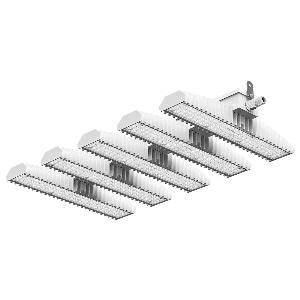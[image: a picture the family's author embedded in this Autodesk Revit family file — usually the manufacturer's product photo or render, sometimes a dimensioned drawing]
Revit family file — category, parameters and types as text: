
# Revit family: 3f_filippi_-_3f_lem_ho_ampio_3f_filippi_-_58958_-_3f_lem_5_ho_led_350_cr_ampio
name_source: partatom
category: Lighting Fixtures
units: mm (PartAtom-declared; Revit-internal decimal feet)

## family parameters
Cut with Voids When Loaded = No
Host = Face
Light Source = No
Part Type = Normal
Room Calculation Point = No
Round Connector Dimension = Use Diameter
Shared = No

## types (1)
- 3F Filippi - 3F LEM HO Ampio (1 x LED, 56516 lm, 345 W, 4000 K)
    Apparent Load = 345 VA
    Approval mark = CE
    CIE Flux Codes = 60 92 99 100 100
    Color Rendering = 80
    Color Temperature = 4000 K
    Control Gear = Electronic ballast
    Default Elevation = 1800 mm
    Description = Industrial luminaire with high light output and high luminous efficiency designed with the most innovative technologies for environments with temperature up to 55°C.

ILLUMINOTECHNICAL
Luminous efficiency 100% (DLOR 100%, ULOR 0%).
Initial luminous flux of the luminaire 56516 lm.
Direct symmetric wide distribution: the illuminated area has a rectangular shape.
Installation Interdistance Transv.D = 1.58 x hu - Long.D = 1.45 x hu.
Tabular UGR (CIE 117 - 4H-8H; S=0.25H; 70/50/20): RUG 24.2 - 25.2.
Beam angle: 93° - 99°.
Luminous efficacy 164 lm/W.
Lifetime (L93/B10): 30000 h. (tq+25°C)
Lifetime (L90/B10): 50000 h. (tq+25°C)
Lifetime (L85/B10): 80000 h. (tq+25°C)
Lifetime (L80/B10): 100000 h. (tq+25°C)
Lifetime (L85/B10): 50000 h. (tq+55°C)
Sudden decreased luminous flux after 50000 hours: 0% (C0).
Photobiological safety in compliance with IEC/TR 62778: RG0 risk exempt, (IEC 62471).
In compliance with IEC/EN 62722-2-1 - IEC/EN 62717 standards.

SOURCE
5 Mid-Power linear LED modules 70W/840.
Energy efficiency class (UE 2019/2020 - UE 2019/2015): C.
CIE 13.3 Colour rendering index: CRI >80 (R9 <50%).
IES TM-30 Fidelity Index: Rf = 84 Rg = 95.
CCT nominal colour temperature 4000 K.
Colour initial tolerance (MacAdam): SDCM 3.

MECHANICAL
Passive modular heatsinks in die-casted aluminium, painted in white colour.
To optimize the thermal management of the LED module, the heatsinks are oversized and provided with self-cleaning of cooling fins.
Wiring body in aluminium and galvanised steel anchored solidly to the sinks and thermally separated.
3F Lens lenses with high luminous efficiency, transparent methacrylate (PMMA), fixed to the LED modules.
Fixing brackets in stainless steel.
Luminaire with limited surface temperature. - D - (EN 60598-2-24)
Dimensions: 952x542 mm, height 129 mm. Weight 21.945 kg.
IP65 protection degree.
Mechanical strength to impacts IK06 (1 joule).
Glow-wire test resistance 650°C.

ELECTRICAL
Halogen Free electronic wiring 230V-50/60Hz, power factor 0.97, THD <25%, constant output current, class I, 3 driver.
Power of the luminaire 345 W.
ENEC - CE.
SAFE FLICKER: PstLM=<1 and SVM=<0.4 (IEC TR 61547-1 and IEC TR 63158), to ensure a more comfortable and safe light.
Luminaire compliant with EN 60598-2-22 for power supply from a centralised emergency system CPSS (Central Power Supply System), not incorporated in the luminaire - high risk areas excluded. The default power and flux are 100% in AC and 100% in DC.
Ambient temperature from -30°C to +55°C.
Temperature class T6 max 85°C.
Quick connection via M20 3P connector with 9-13 mm tightening range.
Power unit positioned on a separate compartment by the LED module to ensure optimum temperatures of cabling components, to be inspectable and maintainable.
Relative humidity UR: <85%.

INSTALLATION
Ceiling / Suspended / Wall.
All accessories dedicated to this product are available on the Catalog and on our website www.3F-Filippi.com.

APPLICATIONS
In commercial environments, exhibition and industrial areas, stores, open areas.
Environments in which it is necessary a total protection against falling fragments (eg environments with foodstuffs or machines with moving parts or with extreme temperature changes), use luminaires with polycarbonate lenses.

WARNING
Fixture not suitable for cold stores with an ambient temperature <0°C and/or relative humidity >85%.
Luminaire designed for disposal/recycling at end-of-life.
Replaceable (LED only) light source by a professional. Replaceable control gear by a professional.
    Height = 129 mm
    Lamp = 1 x LED
    Lamp Light Flux = 56516 lm
    Lamp Power = 345 W
    Lamp count = 1
    Length = 952 mm
    Lifetime = 50000 h
    Luminous efficacy = 164 lm/W
    Manufacturer = 3F Filippi
    ModVariant = No
    Model = 3F Filippi - 58958 - 3F LEM 5 HO LED 350 CR AMPIO
    Mounting Place = Ceiling
    Mounting Type = Pendant
    Number of Poles = 1
    OnlyDefault = Yes
    Power Factor = 1
    Product Name = 3F Filippi - 3F LEM HO Ampio
    Product group = pendant luminaire
    ProductGroupID = 9
    Protection Class = Protection class I
    Protection Degree = IP 65
    RLX_Detail_Level = 1
    RLX_Emergency_Light_Flux = 0 lm
    RLX_Emergency_Type = 0
    RLX_Emergency_Type_DB = No
    RlxData = <blob elided: 132433 chars, md5=542137a1>
    Socket = socket
    Standby Power = 0 W
    System Light Flux = 56516 lm
    System Power = 345 W
    Type Comments = Product without accessories
    Type Image = 3f_filippi_-_lem_5.jpg
    URL = http://relux.com
    VarID = ---
    Voltage = 0 V
    Weight = 0.00 kg
    Width = 542 mm

## geometry (parser evidence)
native form markers: Blend x4, Sweep x11
no freeform markers — native parametric forms only
